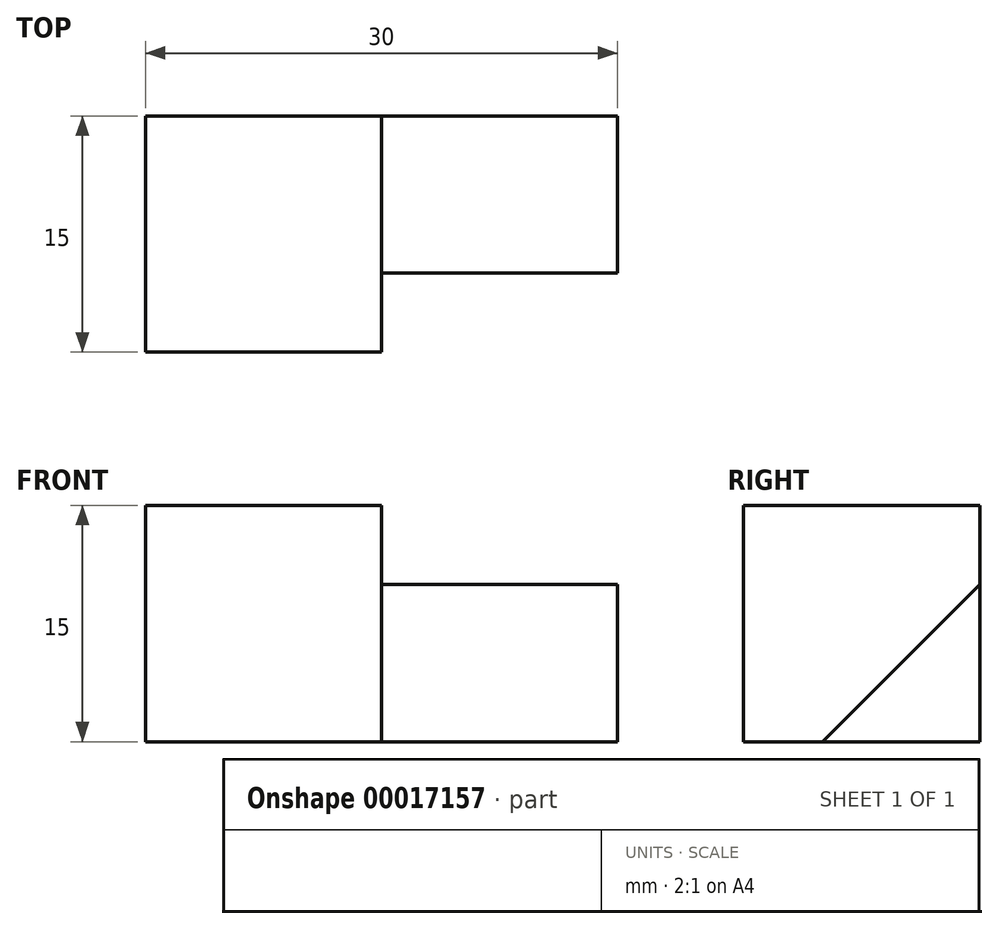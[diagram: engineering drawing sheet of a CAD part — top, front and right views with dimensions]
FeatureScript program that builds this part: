
annotation { "Feature Type Name" : "Feature", "Feature Type Description" : "" }
export const myFeature = defineFeature(function(context is Context, id is Id, definition is map)
    precondition{}
    {
        {
            var Q0;
            Q0=qCreatedBy(makeId("Right.planeOp"),FACE);
            var sketch = newSketch(context, id + "F0", { "sketchPlane" : qUnion([Q0])});
            skLineSegment(sketch, "E0", {"start": v(6.02, 19.52) * mm, "end": v(6.02, 4.52) * mm});
            skLineSegment(sketch, "E1", {"start": v(21.02, 4.52) * mm, "end": v(21.02, 19.52) * mm});
            skLineSegment(sketch, "E2", {"start": v(21.02, 19.52) * mm, "end": v(6.02, 19.52) * mm});
            skLineSegment(sketch, "E3", {"start": v(6.02, 4.52) * mm, "end": v(21.02, 4.52) * mm});
            skLineSegment(sketch, "E4", {"start": v(21.02, 14.52) * mm, "end": v(11.02, 4.52) * mm});
            skSolve(sketch);
        }
        {
            var Q0;
            Q0=makeQuery(id+"F0.imprint","IMPRINT",FACE,{"disambiguationData":[TD([[makeQuery(id+"F0.imprint","IMPRINT",EDGE,{"derivedFrom":sQuery(id+"F0.wireOp",EDGE,"E0")}),1.0]])]});
            var Q1;
            {var subQ1=sQuery(id+"F0.wireOp",EDGE,"E3");Q1=makeQuery(id+"F0.imprint","IMPRINT",FACE,{"disambiguationData":[TD([[makeQuery(id+"F0.imprint","IMPRINT",EDGE,{"derivedFrom":subQ1}),1.0]])]});}
            extrude(context, id + "F1", {"entities" : qUnion([Q0, Q1]), "depth" : 15 * mm});
        }
        {
            var Q0;
            {var subQ0=sQuery(id+"F0.wireOp",EDGE,"E4");Q0=makeQuery(id+"F0.imprint","IMPRINT",FACE,{"disambiguationData":[TD([[makeQuery(id+"F0.imprint","IMPRINT",EDGE,{"derivedFrom":subQ0}),1.0]])]});}
            extrude(context, id + "F2", {"entities" : qUnion([Q0]), "operationType" : NewBodyOperationType.ADD, "depth" : 30 * mm});
        }
    });
